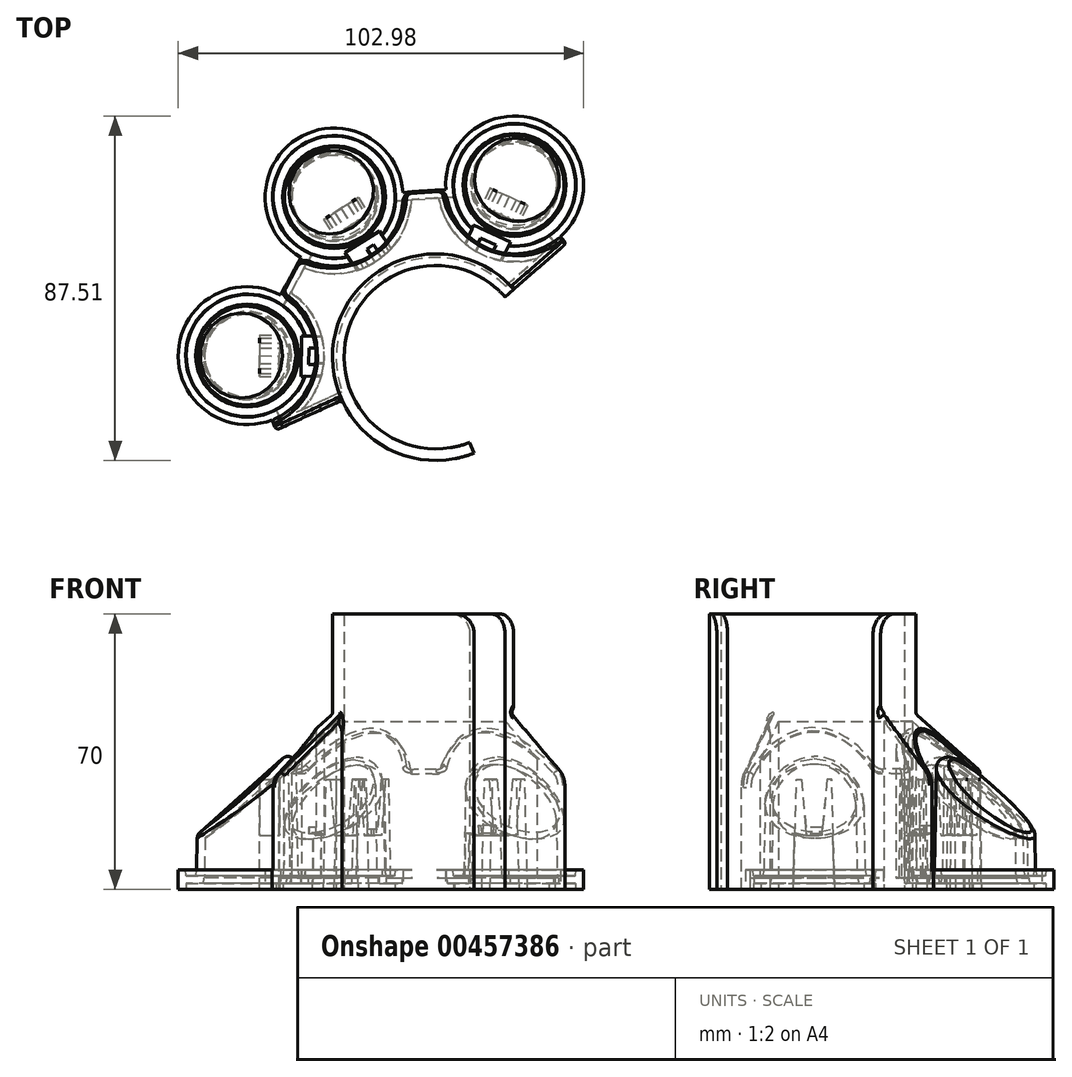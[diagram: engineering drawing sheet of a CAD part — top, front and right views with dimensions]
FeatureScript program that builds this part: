
annotation { "Feature Type Name" : "Feature", "Feature Type Description" : "" }
export const myFeature = defineFeature(function(context is Context, id is Id, definition is map)
    precondition{}
    {
        {
            var Q0;
            Q0=qCreatedBy(makeId("Top.planeOp"),FACE);
            var sketch = newSketch(context, id + "F0", { "sketchPlane" : qUnion([Q0])});
            skCircle(sketch, "E0", {"center": v(0, 0) * mm, "radius": 23.31 * mm});
            skCircle(sketch, "E1", {"center": v(0, 0) * mm, "radius": 26.24 * mm});
            skCircle(sketch, "E2", {"center": v(-47.92, 0.4) * mm, "radius": 12.92 * mm});
            skCircle(sketch, "E3", {"center": v(-47.92, 0.4) * mm, "radius": 17.52 * mm});
            skCircle(sketch, "E4.1.0", {"center": v(-25.82, 40.7) * mm, "radius": 17.52 * mm});
            skCircle(sketch, "E4.1.1", {"center": v(-25.82, 40.7) * mm, "radius": 12.92 * mm});
            skCircle(sketch, "E4.2.0", {"center": v(20.02, 43.75) * mm, "radius": 17.52 * mm});
            skCircle(sketch, "E4.2.1", {"center": v(20.02, 43.75) * mm, "radius": 12.92 * mm});
            skPoint(sketch, "E4.center", {"position": v(-0.1, 0.38) * mm});
            skLineSegment(sketch, "E4.anchor1", {"start": v(-0.1, 0.38) * mm, "end": v(-47.92, 0.4) * mm, "construction": true});
            skLineSegment(sketch, "E4.anchor2", {"start": v(-0.1, 0.38) * mm, "end": v(20.02, 43.75) * mm, "construction": true});
            skLineSegment(sketch, "E5", {"start": v(-39.5, 15.77) * mm, "end": v(-34.25, 25.33) * mm});
            skLineSegment(sketch, "E6", {"start": v(-8.34, 41.86) * mm, "end": v(2.54, 42.58) * mm});
            skLineSegment(sketch, "E7", {"start": v(17.58, 15.31) * mm, "end": v(19.79, 17.23) * mm});
            skLineSegment(sketch, "E8", {"start": v(8.61, -21.66) * mm, "end": v(9.7, -24.38) * mm});
            skLineSegment(sketch, "E9", {"start": v(31.65, 30.65) * mm, "end": v(33.19, 28.9) * mm});
            skLineSegment(sketch, "E10", {"start": v(33.19, 28.9) * mm, "end": v(19.79, 17.23) * mm});
            skLineSegment(sketch, "E11", {"start": v(-41.63, -15.94) * mm, "end": v(-40.62, -18.56) * mm});
            skLineSegment(sketch, "E12", {"start": v(-40.62, -18.56) * mm, "end": v(-23.87, -10.9) * mm});
            skLineSegment(sketch, "E13", {"start": v(-8.34, 41.86) * mm, "end": v(-34.25, 25.33) * mm});
            skSolve(sketch);
        }
        {
            var Q0;
            {var subQ0=sQuery(id+"F0.wireOp",EDGE,"E7");Q0=makeQuery(id+"F0.imprint","IMPRINT",FACE,{"disambiguationData":[TD([[makeQuery(id+"F0.imprint","IMPRINT",EDGE,{"derivedFrom":subQ0}),1.0]])]});}
            var Q1;
            {var subQ0=sQuery(id+"F0.wireOp",EDGE,"E5");Q1=makeQuery(id+"F0.imprint","IMPRINT",FACE,{"disambiguationData":[TD([[makeQuery(id+"F0.imprint","IMPRINT",EDGE,{"derivedFrom":subQ0}),-1.0]])]});}
            var Q2;
            Q2=makeQuery(id+"F0.imprint","IMPRINT",FACE,{"disambiguationData":[TD([[makeQuery(id+"F0.imprint","IMPRINT",EDGE,{"derivedFrom":sQuery(id+"F0.wireOp",EDGE,"E4.2.1")}),-1.0]])]});
            var Q3;
            Q3=makeQuery(id+"F0.imprint","IMPRINT",FACE,{"disambiguationData":[TD([[makeQuery(id+"F0.imprint","IMPRINT",EDGE,{"derivedFrom":sQuery(id+"F0.wireOp",EDGE,"E4.2.1")}),1.0]])]});
            var Q4;
            Q4=makeQuery(id+"F0.imprint","IMPRINT",FACE,{"disambiguationData":[TD([[makeQuery(id+"F0.imprint","IMPRINT",EDGE,{"derivedFrom":sQuery(id+"F0.wireOp",EDGE,"E4.1.1")}),-1.0]])]});
            var Q5;
            Q5=makeQuery(id+"F0.imprint","IMPRINT",FACE,{"disambiguationData":[TD([[makeQuery(id+"F0.imprint","IMPRINT",EDGE,{"derivedFrom":sQuery(id+"F0.wireOp",EDGE,"E4.1.1")}),1.0]])]});
            var Q6;
            Q6=makeQuery(id+"F0.imprint","IMPRINT",FACE,{"disambiguationData":[TD([[makeQuery(id+"F0.imprint","IMPRINT",EDGE,{"derivedFrom":sQuery(id+"F0.wireOp",EDGE,"E2")}),1.0]])]});
            var Q7;
            Q7=makeQuery(id+"F0.imprint","IMPRINT",FACE,{"disambiguationData":[TD([[makeQuery(id+"F0.imprint","IMPRINT",EDGE,{"derivedFrom":sQuery(id+"F0.wireOp",EDGE,"E2")}),-1.0]])]});
            extrude(context, id + "F1", {"entities" : qUnion([Q0, Q1, Q2, Q3, Q4, Q5, Q6, Q7]), "depth" : 5 * mm});
        }
        {
            var Q0;
            {var subQ5=sQuery(id+"F0.wireOp",EDGE,"zP7nwWVG-uyIf-8n9z-kM4t-hGhugBOlDqZd");Q0=makeQuery(id+"F0.imprint","IMPRINT",FACE,{"disambiguationData":[TD([[makeQuery(id+"F0.imprint","IMPRINT",EDGE,{"derivedFrom":subQ5}),-1.0]])]});}
            var Q1;
            {var subQ4=sQuery(id+"F0.wireOp",EDGE,"E7");Q1=makeQuery(id+"F0.imprint","IMPRINT",FACE,{"disambiguationData":[TD([[makeQuery(id+"F0.imprint","IMPRINT",EDGE,{"derivedFrom":subQ4}),1.0]])]});}
            var Q2;
            {var subQ0=sQuery(id+"F0.wireOp",EDGE,"E0");var subQ1=makeQuery(id+"F0.imprint","INTERSECT",VERTEX,{"derivedFrom":[subQ0,sQuery(id+"F0.wireOp",EDGE,"E7")]});Q2=makeQuery(id+"F0.imprint","IMPRINT",FACE,{"disambiguationData":[TD([[makeQuery(id+"F0.imprint","IMPRINT",EDGE,{"disambiguationData":[TD([[subQ1,-1.0]])],"derivedFrom":subQ0}),1.0]])]});}
            var Q3;
            {var subQ0=sQuery(id+"F0.wireOp",EDGE,"E5");Q3=makeQuery(id+"F0.imprint","IMPRINT",FACE,{"disambiguationData":[TD([[makeQuery(id+"F0.imprint","IMPRINT",EDGE,{"derivedFrom":subQ0}),-1.0]])]});}
            var Q4;
            Q4=makeQuery(id+"F1.opExtrude","CAP_FACE",FACE,{"disambiguationData":[OSD([sQuery(id+"F0.wireOp",EDGE,"E1"),sQuery(id+"F0.wireOp",EDGE,"E3"),sQuery(id+"F0.wireOp",EDGE,"E4.1.0"),sQuery(id+"F0.wireOp",EDGE,"E4.2.0"),sQuery(id+"F0.wireOp",EDGE,"zP7nwWVG-uyIf-8n9z-kM4t-hGhugBOlDqZd"),sQuery(id+"F0.wireOp",EDGE,"U5mlmDiE-PqSx-qM5O-4Tfx-D3ZpNaptZaIW"),sQuery(id+"F0.wireOp",EDGE,"E5"),sQuery(id+"F0.wireOp",EDGE,"E6")])],"isStart":false});
            extrude(context, id + "F2", {"entities" : qUnion([Q0, Q1, Q2, Q3]), "operationType" : NewBodyOperationType.ADD, "depth" : 70 * mm, "hasSecondDirection" : true, "secondDirectionBound" : SecondDirectionBoundingType.UP_TO_SURFACE, "secondDirectionOppositeDirection" : false, "secondDirectionBoundEntityFace" : qUnion([Q4]), "secondDirectionDepth" : 25 * mm});
        }
        {
            var Q0;
            Q0=makeQuery(id+"F0.imprint","IMPRINT",FACE,{"disambiguationData":[TD([[makeQuery(id+"F0.imprint","IMPRINT",EDGE,{"derivedFrom":sQuery(id+"F0.wireOp",EDGE,"E4.2.1")}),1.0]])]});
            var Q1;
            Q1=makeQuery(id+"F0.imprint","IMPRINT",FACE,{"disambiguationData":[TD([[makeQuery(id+"F0.imprint","IMPRINT",EDGE,{"derivedFrom":sQuery(id+"F0.wireOp",EDGE,"E4.1.1")}),1.0]])]});
            var Q2;
            Q2=makeQuery(id+"F0.imprint","IMPRINT",FACE,{"disambiguationData":[TD([[makeQuery(id+"F0.imprint","IMPRINT",EDGE,{"derivedFrom":sQuery(id+"F0.wireOp",EDGE,"E2")}),1.0]])]});
            extrude(context, id + "F3", {"entities" : qUnion([Q0, Q1, Q2]), "operationType" : NewBodyOperationType.ADD, "depth" : 53.8 * mm, "hasDraft" : true, "draftAngle" : 1 * degree, "draftPullDirection" : true});
        }
        {
            var Q0;
            {var subQ0=sQuery(id+"F0.wireOp",EDGE,"E0");var subQ1=makeQuery(id+"F0.imprint","INTERSECT",VERTEX,{"derivedFrom":[subQ0,sQuery(id+"F0.wireOp",EDGE,"E7")]});Q0=makeQuery(id+"F0.imprint","IMPRINT",FACE,{"disambiguationData":[TD([[makeQuery(id+"F0.imprint","IMPRINT",EDGE,{"disambiguationData":[TD([[subQ1,-1.0]])],"derivedFrom":subQ0}),1.0]])]});}
            var Q1;
            Q1=sQuery(id+"F0.wireOp",EDGE,"E0");
            extrude(context, id + "F4", {"entities" : qUnion([Q0]), "operationType" : NewBodyOperationType.REMOVE, "surfaceEntities" : qUnion([Q1]), "endBound" : BoundingType.THROUGH_ALL, "depth" : 25 * mm});
        }
        {
            var Q0;
            {var subQ0=sQuery(id+"F0.wireOp",EDGE,"E10");var subQ1=sQuery(id+"F0.wireOp",EDGE,"E7");Q0=makeQuery(id+"F2.boolean.opBoolean","MERGE",FACE,{"derivedFrom":[makeQuery(id+"F1.opExtrude","SWEPT_FACE",FACE,{"disambiguationData":[OSD([subQ1,subQ0])]}),makeQuery(id+"F2.opExtrude","SWEPT_FACE",FACE,{"disambiguationData":[OSD([subQ1,subQ0])]})]});}
            var sketch = newSketch(context, id + "F5", { "sketchPlane" : qUnion([Q0])});
            skLineSegment(sketch, "E14", {"start": v(26.24, 44.56) * mm, "end": v(67.38, 7.9) * mm});
            skLineSegment(sketch, "E15", {"start": v(67.38, 7.9) * mm, "end": v(67.38, 70) * mm});
            skLineSegment(sketch, "E16", {"start": v(67.38, 70) * mm, "end": v(26.24, 70) * mm});
            skLineSegment(sketch, "E17", {"start": v(26.24, 44.56) * mm, "end": v(26.24, 70) * mm});
            skPoint(sketch, "E18.0.end.orphan", {"position": v(26.24, 0) * mm});
            skPoint(sketch, "E18.0.start.orphan", {"position": v(-26.24, 0) * mm});
            skSolve(sketch);
        }
        {
            var Q0;
            {var subQ0=sQuery(id+"F5.wireOp",EDGE,"E17");Q0=makeQuery(id+"F5.imprint","IMPRINT",FACE,{"disambiguationData":[TD([[makeQuery(id+"F5.imprint","IMPRINT",EDGE,{"derivedFrom":subQ0}),-1.0]])]});}
            var Q1;
            {var subQ0=sQuery(id+"F5.wireOp",EDGE,"E15");Q1=makeQuery(id+"F5.imprint","IMPRINT",FACE,{"disambiguationData":[TD([[makeQuery(id+"F5.imprint","IMPRINT",EDGE,{"derivedFrom":subQ0}),1.0]])]});}
            var Q2;
            Q2=sQuery(id+"F0.wireOp",EDGE,"E0");
            revolve(context, id + "F6", {"operationType" : NewBodyOperationType.REMOVE, "entities" : qUnion([Q0, Q1]), "axis" : qUnion([Q2]), "revolveType" : RevolveType.FULL, "oppositeDirection" : true});
        }
        {
            var Q0;
            Q0=sQuery(id+"F0.wireOp",EDGE,"E13");
            extrude(context, id + "F7", {"bodyType" : ToolBodyType.SURFACE, "surfaceEntities" : qUnion([Q0]), "depth" : 101.5 * mm});
        }
        {
            var Q0;
            Q0=makeQuery(id+"F7.opExtrude","SWEPT_FACE",FACE,{"disambiguationData":[OSD([sQuery(id+"F0.wireOp",EDGE,"E13")])]});
            var sketch = newSketch(context, id + "F8", { "sketchPlane" : qUnion([Q0])});
            skFitSpline(sketch, "E19.0.0", {"points": [v(1.38, 35.88) * mm, v(0.16, 35.97) * mm, v(-0.81, 35.93) * mm, v(-1.76, 35.84) * mm, v(-2.69, 35.64) * mm, v(-3.59, 35.36) * mm, v(-4.45, 35.04) * mm, v(-5.47, 34.55) * mm, v(-6.6, 33.86) * mm, v(-7.6, 33.1) * mm, v(-8.52, 32.28) * mm, v(-9.34, 31.4) * mm, v(-10.07, 30.5) * mm, v(-10.9, 29.28) * mm, v(-11.57, 28.03) * mm, v(-12.06, 26.75) * mm, v(-12.43, 25.47) * mm, v(-12.62, 24.2) * mm, v(-12.63, 22.96) * mm, v(-12.5, 21.71) * mm, v(-12.1, 20.23) * mm, v(-11.37, 18.83) * mm, v(-10.53, 17.76) * mm, v(-9.8, 17) * mm, v(-9.1, 16.43) * mm, v(-8.47, 16) * mm, v(-7.8, 15.58) * mm, v(-6.9, 15.1) * mm, v(-5.93, 14.7) * mm, v(-5.09, 14.42) * mm, v(-4.21, 14.17) * mm, v(-3.1, 13.93) * mm, v(-1.7, 13.75) * mm, v(-0.23, 13.68) * mm, v(0.96, 13.72) * mm, v(1.91, 13.82) * mm, v(2.62, 13.91) * mm, v(3.32, 14.04) * mm, v(4.21, 14.25) * mm, v(5.29, 14.56) * mm, v(6.5, 15.04) * mm, v(7.59, 15.6) * mm, v(8.58, 16.23) * mm, v(9.45, 16.93) * mm, v(10.2, 17.67) * mm, v(10.84, 18.47) * mm, v(11.37, 19.3) * mm, v(11.78, 20.16) * mm, v(12.09, 21.05) * mm, v(12.3, 21.97) * mm, v(12.4, 22.9) * mm, v(12.4, 23.83) * mm, v(12.32, 24.78) * mm, v(12.14, 25.75) * mm, v(11.87, 26.7) * mm, v(11.39, 27.98) * mm, v(10.74, 29.23) * mm, v(9.9, 30.48) * mm, v(9.18, 31.38) * mm, v(8.37, 32.25) * mm, v(7.46, 33.07) * mm, v(6.44, 33.85) * mm, v(5.33, 34.53) * mm, v(4.3, 35.03) * mm, v(3.44, 35.36) * mm, v(2.54, 35.64) * mm, v(1.38, 35.88) * mm, v(0.16, 35.97) * mm, v(-0.81, 35.93) * mm, v(1.38, 35.88) * mm]});
            skLineSegment(sketch, "E20", {"start": v(-12.95, 5) * mm, "end": v(-12.62, 23.55) * mm});
            skLineSegment(sketch, "E21", {"start": v(12.4, 23.6) * mm, "end": v(12.72, 5) * mm});
            skLineSegment(sketch, "E22.0", {"start": v(-15.48, 0) * mm, "end": v(15.25, 0) * mm});
            skLineSegment(sketch, "E23", {"start": v(0, 45.7) * mm, "end": v(0, 0) * mm});
            skLineSegment(sketch, "E24", {"start": v(5.25, 0) * mm, "end": v(4.46, 28) * mm});
            skLineSegment(sketch, "E25", {"start": v(4.46, 28) * mm, "end": v(3.27, 27.98) * mm});
            skLineSegment(sketch, "E26", {"start": v(3.27, 27.98) * mm, "end": v(1.95, 13.8) * mm});
            skLineSegment(sketch, "E27", {"start": v(1.95, 13.8) * mm, "end": v(0, 13.77) * mm});
            skLineSegment(sketch, "E28.MirrorCS", {"start": v(-1.95, 13.8) * mm, "end": v(0, 13.77) * mm});
            skLineSegment(sketch, "E29.MirrorCS", {"start": v(-3.27, 27.98) * mm, "end": v(-1.95, 13.8) * mm});
            skLineSegment(sketch, "E30.MirrorCS", {"start": v(-4.46, 28) * mm, "end": v(-3.27, 27.98) * mm});
            skLineSegment(sketch, "E31.MirrorCS", {"start": v(-5.25, 0) * mm, "end": v(-4.46, 28) * mm});
            skLineSegment(sketch, "E32", {"start": v(-2.09, 15.29) * mm, "end": v(2.09, 15.29) * mm});
            skSolve(sketch);
        }
        {
            var Q0;
            Q0=makeQuery(id+"F2.opExtrude","SWEPT_EDGE",EDGE,{"disambiguationData":[OSD([sQuery(id+"F0.wireOp",EDGE,"E4.1.0"),sQuery(id+"F0.wireOp",EDGE,"E5"),sQuery(id+"F0.wireOp",EDGE,"E13")])]});
            var Q1;
            Q1=makeQuery(id+"F2.opExtrude","SWEPT_EDGE",EDGE,{"disambiguationData":[OSD([sQuery(id+"F0.wireOp",EDGE,"E4.1.0"),sQuery(id+"F0.wireOp",EDGE,"E6"),sQuery(id+"F0.wireOp",EDGE,"E13")])]});
            var Q2;
            Q2=makeQuery(id+"F2.opExtrude","SWEPT_EDGE",EDGE,{"disambiguationData":[OSD([sQuery(id+"F0.wireOp",EDGE,"E4.2.0"),sQuery(id+"F0.wireOp",EDGE,"E6")])]});
            var Q3;
            Q3=makeQuery(id+"F2.opExtrude","SWEPT_EDGE",EDGE,{"disambiguationData":[OSD([sQuery(id+"F0.wireOp",EDGE,"E3"),sQuery(id+"F0.wireOp",EDGE,"E5")])]});
            fillet(context, id + "F9", {"entities" : qUnion([Q0, Q1, Q2, Q3]), "radius" : 2.5 * mm, "tangentPropagation" : true, "allowEdgeOverflow" : false});
        }
        {
            var Q0;
            {var subQ0=sQuery(id+"F0.wireOp",EDGE,"E11");Q0=makeQuery(id+"F6.boolean.opBoolean","INTERSECT",EDGE,{"derivedFrom":[makeQuery(id+"F2.boolean.opBoolean","MERGE",FACE,{"derivedFrom":[makeQuery(id+"F1.opExtrude","SWEPT_FACE",FACE,{"disambiguationData":[OSD([subQ0])]}),makeQuery(id+"F2.opExtrude","SWEPT_FACE",FACE,{"disambiguationData":[OSD([subQ0])]})]}),makeQuery(id+"F6.opRevolve","SWEPT_FACE",FACE,{"disambiguationData":[OSD([sQuery(id+"F5.wireOp",EDGE,"E14")])]})]});}
            var Q1;
            {var subQ0=sQuery(id+"F0.wireOp",EDGE,"E9");Q1=makeQuery(id+"F6.boolean.opBoolean","INTERSECT",EDGE,{"derivedFrom":[makeQuery(id+"F2.boolean.opBoolean","MERGE",FACE,{"derivedFrom":[makeQuery(id+"F1.opExtrude","SWEPT_FACE",FACE,{"disambiguationData":[OSD([subQ0])]}),makeQuery(id+"F2.opExtrude","SWEPT_FACE",FACE,{"disambiguationData":[OSD([subQ0])]})]}),makeQuery(id+"F6.opRevolve","SWEPT_FACE",FACE,{"disambiguationData":[OSD([sQuery(id+"F5.wireOp",EDGE,"E14")])]})]});}
            var Q2;
            Q2=makeQuery(id+"F2.opExtrude","CAP_EDGE",EDGE,{"disambiguationData":[OSD([sQuery(id+"F0.wireOp",EDGE,"E7"),sQuery(id+"F0.wireOp",EDGE,"E10")])],"isStart":false});
            var Q3;
            Q3=makeQuery(id+"F2.opExtrude","CAP_EDGE",EDGE,{"disambiguationData":[OSD([sQuery(id+"F0.wireOp",EDGE,"E8")])],"isStart":false});
            fillet(context, id + "F10", {"entities" : qUnion([Q0, Q1, Q2, Q3]), "radius" : 5 * mm, "tangentPropagation" : true, "allowEdgeOverflow" : false});
        }
        {
            var Q0;
            {var subQ0=sQuery(id+"F0.wireOp",EDGE,"E1");Q0=makeQuery(id+"F6.boolean.opBoolean","COPY",FACE,{"disambiguationData":[TD([makeQuery(id+"F1.opExtrude","SWEPT_FACE",FACE,{"disambiguationData":[OSD([subQ0])]})])],"derivedFrom":makeQuery(id+"F6.opRevolve","SWEPT_FACE",FACE,{"disambiguationData":[OSD([sQuery(id+"F5.wireOp",EDGE,"E14")])]})});}
            fillet(context, id + "F11", {"entities" : qUnion([Q0]), "radius" : 1 * mm, "tangentPropagation" : true, "allowEdgeOverflow" : false});
        }
        {
            var Q0;
            Q0=makeQuery(id+"F6.boolean.opBoolean","COPY",FACE,{"disambiguationData":[TD([makeQuery(id+"F3.opExtrude","SWEPT_FACE",FACE,{"disambiguationData":[OSD([sQuery(id+"F0.wireOp",EDGE,"E2")])]})])],"derivedFrom":makeQuery(id+"F6.opRevolve","SWEPT_FACE",FACE,{"disambiguationData":[OSD([sQuery(id+"F5.wireOp",EDGE,"E14")])]})});
            var Q1;
            Q1=makeQuery(id+"F6.boolean.opBoolean","COPY",FACE,{"disambiguationData":[TD([makeQuery(id+"F3.opExtrude","SWEPT_FACE",FACE,{"disambiguationData":[OSD([sQuery(id+"F0.wireOp",EDGE,"E4.1.1")])]})])],"derivedFrom":makeQuery(id+"F6.opRevolve","SWEPT_FACE",FACE,{"disambiguationData":[OSD([sQuery(id+"F5.wireOp",EDGE,"E14")])]})});
            var Q2;
            Q2=makeQuery(id+"F6.boolean.opBoolean","COPY",FACE,{"disambiguationData":[TD([makeQuery(id+"F3.opExtrude","SWEPT_FACE",FACE,{"disambiguationData":[OSD([sQuery(id+"F0.wireOp",EDGE,"E4.2.1")])]})])],"derivedFrom":makeQuery(id+"F6.opRevolve","SWEPT_FACE",FACE,{"disambiguationData":[OSD([sQuery(id+"F5.wireOp",EDGE,"E14")])]})});
            fillet(context, id + "F12", {"entities" : qUnion([Q0, Q1, Q2]), "radius" : 2 * mm, "tangentPropagation" : true, "allowEdgeOverflow" : false});
        }
        {
            var Q0;
            {var subQ0=sQuery(id+"F0.wireOp",EDGE,"E11");var subQ1=sQuery(id+"F0.wireOp",EDGE,"E5");var subQ2=sQuery(id+"F0.wireOp",EDGE,"E3");Q0=makeQuery(id+"F2.boolean.opBoolean","SPLIT",FACE,{"disambiguationData":[TD([makeQuery(id+"F1.opExtrude","SWEPT_FACE",FACE,{"disambiguationData":[OSD([subQ2])]})])],"derivedFrom":makeQuery(id+"F1.opExtrude","CAP_FACE",FACE,{"disambiguationData":[OSD([sQuery(id+"F0.wireOp",EDGE,"E0"),sQuery(id+"F0.wireOp",EDGE,"E1"),subQ2,sQuery(id+"F0.wireOp",EDGE,"E4.1.0"),sQuery(id+"F0.wireOp",EDGE,"E4.2.0"),subQ1,sQuery(id+"F0.wireOp",EDGE,"E6"),sQuery(id+"F0.wireOp",EDGE,"E7"),sQuery(id+"F0.wireOp",EDGE,"E8"),sQuery(id+"F0.wireOp",EDGE,"E9"),sQuery(id+"F0.wireOp",EDGE,"E10"),subQ0,sQuery(id+"F0.wireOp",EDGE,"E12")])],"isStart":false})});}
            var sketch = newSketch(context, id + "F13", { "sketchPlane" : qUnion([Q0])});
            skArc(sketch, "E33.0.0", {"start": v(-39.5, 15.77) * mm, "mid": v(-65.4, 1.59) * mm, "end": v(-41.63, -15.94) * mm});
            skLineSegment(sketch, "E33.0.1", {"start": v(-41.63, -15.94) * mm, "end": v(-41.28, -16.85) * mm});
            skArc(sketch, "E33.0.2", {"start": v(-41.28, -16.85) * mm, "mid": v(-41.27, -16.1) * mm, "end": v(-40.76, -15.58) * mm});
            skArc(sketch, "E33.0.3", {"start": v(-40.76, -15.58) * mm, "mid": v(-30.5, -1.39) * mm, "end": v(-37.64, 14.6) * mm});
            skArc(sketch, "E33.0.4", {"start": v(-37.64, 14.6) * mm, "mid": v(-38.62, 16.07) * mm, "end": v(-38.37, 17.82) * mm});
            skLineSegment(sketch, "E33.0.5", {"start": v(-38.37, 17.82) * mm, "end": v(-39.5, 15.77) * mm});
            skArc(sketch, "E34.0.0", {"start": v(-8.34, 41.86) * mm, "mid": v(-35.25, 55.46) * mm, "end": v(-34.25, 25.33) * mm});
            skLineSegment(sketch, "E34.0.1", {"start": v(-34.25, 25.33) * mm, "end": v(-35.38, 23.28) * mm});
            skArc(sketch, "E34.0.2", {"start": v(-35.38, 23.28) * mm, "mid": v(-34.03, 24.42) * mm, "end": v(-32.27, 24.4) * mm});
            skArc(sketch, "E34.0.3", {"start": v(-32.27, 24.4) * mm, "mid": v(-16.4, 25.92) * mm, "end": v(-8.33, 39.67) * mm});
            skArc(sketch, "E34.0.4", {"start": v(-8.33, 39.67) * mm, "mid": v(-7.61, 41.28) * mm, "end": v(-6, 42.01) * mm});
            skLineSegment(sketch, "E34.0.5", {"start": v(-6, 42.01) * mm, "end": v(-8.34, 41.86) * mm});
            skArc(sketch, "E35.0.0", {"start": v(31.65, 30.65) * mm, "mid": v(26.67, 59.96) * mm, "end": v(2.54, 42.58) * mm});
            skLineSegment(sketch, "E35.0.1", {"start": v(2.54, 42.58) * mm, "end": v(0.2, 42.43) * mm});
            skArc(sketch, "E35.0.2", {"start": v(0.2, 42.43) * mm, "mid": v(1.9, 41.91) * mm, "end": v(2.82, 40.41) * mm});
            skArc(sketch, "E35.0.3", {"start": v(2.82, 40.41) * mm, "mid": v(13.95, 27.32) * mm, "end": v(30.92, 30.04) * mm});
            skArc(sketch, "E35.0.4", {"start": v(30.92, 30.04) * mm, "mid": v(31.63, 30.25) * mm, "end": v(32.3, 29.92) * mm});
            skLineSegment(sketch, "E35.0.5", {"start": v(32.3, 29.92) * mm, "end": v(31.65, 30.65) * mm});
            skCircle(sketch, "E36.0", {"center": v(-47.92, 0.4) * mm, "radius": 12.92 * mm});
            skCircle(sketch, "E37.0", {"center": v(-25.82, 40.7) * mm, "radius": 12.92 * mm});
            skCircle(sketch, "E38.0", {"center": v(20.02, 43.75) * mm, "radius": 12.92 * mm});
            skCircle(sketch, "E39.0", {"center": v(-47.92, 0.4) * mm, "radius": 15.62 * mm});
            skCircle(sketch, "E40.0", {"center": v(-25.82, 40.7) * mm, "radius": 15.62 * mm});
            skCircle(sketch, "E41.0", {"center": v(20.02, 43.75) * mm, "radius": 15.62 * mm});
            skSolve(sketch);
        }
        {
            var Q0;
            Q0=makeQuery(id+"F13.imprint","IMPRINT",FACE,{"disambiguationData":[TD([[makeQuery(id+"F13.imprint","IMPRINT",EDGE,{"derivedFrom":sQuery(id+"F13.wireOp",EDGE,"E38.0")}),-1.0]])]});
            var Q1;
            Q1=makeQuery(id+"F13.imprint","IMPRINT",FACE,{"disambiguationData":[TD([[makeQuery(id+"F13.imprint","IMPRINT",EDGE,{"derivedFrom":sQuery(id+"F13.wireOp",EDGE,"E37.0")}),-1.0]])]});
            var Q2;
            Q2=makeQuery(id+"F13.imprint","IMPRINT",FACE,{"disambiguationData":[TD([[makeQuery(id+"F13.imprint","IMPRINT",EDGE,{"derivedFrom":sQuery(id+"F13.wireOp",EDGE,"E36.0")}),-1.0]])]});
            extrude(context, id + "F14", {"entities" : qUnion([Q0, Q1, Q2]), "operationType" : NewBodyOperationType.REMOVE, "oppositeDirection" : true, "depth" : 1.5 * mm, "hasDraft" : true, "draftAngle" : 5 * degree, "draftPullDirection" : true});
        }
        {
            var Q0;
            Q0=makeQuery(id+"F1.opExtrude","CAP_FACE",FACE,{"disambiguationData":[OSD([sQuery(id+"F0.wireOp",EDGE,"E0"),sQuery(id+"F0.wireOp",EDGE,"E1"),sQuery(id+"F0.wireOp",EDGE,"E3"),sQuery(id+"F0.wireOp",EDGE,"E4.1.0"),sQuery(id+"F0.wireOp",EDGE,"E4.2.0"),sQuery(id+"F0.wireOp",EDGE,"E5"),sQuery(id+"F0.wireOp",EDGE,"E6"),sQuery(id+"F0.wireOp",EDGE,"E7"),sQuery(id+"F0.wireOp",EDGE,"E8"),sQuery(id+"F0.wireOp",EDGE,"E9"),sQuery(id+"F0.wireOp",EDGE,"E10"),sQuery(id+"F0.wireOp",EDGE,"E11"),sQuery(id+"F0.wireOp",EDGE,"E12")])],"isStart":true});
            shell(context, id + "F15", {"entities" : qUnion([Q0]), "thickness" : 2 * mm});
        }
        {
            var Q0;
            {var subQ0=sQuery(id+"F8.wireOp",EDGE,"E31.MirrorCS");var subQ1=sQuery(id+"F8.wireOp",EDGE,"E19.0.0");var subQ2=makeQuery(id+"F8.imprint","INTERSECT",VERTEX,{"derivedFrom":[subQ1,subQ0]});Q0=makeQuery(id+"F8.imprint","IMPRINT",FACE,{"disambiguationData":[TD([[makeQuery(id+"F8.imprint","IMPRINT",EDGE,{"disambiguationData":[TD([[subQ2,-1.0]])],"derivedFrom":subQ1}),-1.0]])]});}
            var Q1;
            {var subQ5=sQuery(id+"F8.wireOp",EDGE,"E25");Q1=makeQuery(id+"F8.imprint","IMPRINT",FACE,{"disambiguationData":[TD([[makeQuery(id+"F8.imprint","IMPRINT",EDGE,{"derivedFrom":subQ5}),1.0]])]});}
            var Q2;
            {var subQ0=sQuery(id+"F8.wireOp",EDGE,"E28.MirrorCS");Q2=makeQuery(id+"F8.imprint","IMPRINT",FACE,{"disambiguationData":[TD([[makeQuery(id+"F8.imprint","IMPRINT",EDGE,{"derivedFrom":subQ0}),-1.0]])]});}
            var Q3;
            {var subQ0=sQuery(id+"F8.wireOp",EDGE,"E23");var subQ5=sQuery(id+"F8.wireOp",EDGE,"E19.0.0");var subQ6=makeQuery(id+"F8.imprint","INTERSECT",VERTEX,{"disambiguationData":[OD(1.0)],"derivedFrom":[subQ5,subQ0]});Q3=makeQuery(id+"F8.imprint","IMPRINT",FACE,{"disambiguationData":[TD([[makeQuery(id+"F8.imprint","IMPRINT",EDGE,{"disambiguationData":[TD([[subQ6,-1.0]])],"derivedFrom":subQ5}),-1.0]])]});}
            var Q4;
            Q4=sQuery(id+"F8.wireOp",EDGE,"E24");
            extrude(context, id + "F16", {"entities" : qUnion([Q0, Q1, Q2, Q3]), "surfaceEntities" : qUnion([Q4]), "depth" : 5 * mm});
        }
        {
            var Q0;
            Q0=makeQuery(id+"F16.opExtrude","SWEPT_BODY",BODY,{"disambiguationData":[OSD([sQuery(id+"F8.wireOp",EDGE,"E19.0.0"),sQuery(id+"F8.wireOp",EDGE,"E22.0"),sQuery(id+"F8.wireOp",EDGE,"E23"),sQuery(id+"F8.wireOp",EDGE,"E24"),sQuery(id+"F8.wireOp",EDGE,"E25"),sQuery(id+"F8.wireOp",EDGE,"E26"),sQuery(id+"F8.wireOp",EDGE,"E27"),sQuery(id+"F8.wireOp",EDGE,"E28.MirrorCS"),sQuery(id+"F8.wireOp",EDGE,"E29.MirrorCS"),sQuery(id+"F8.wireOp",EDGE,"E30.MirrorCS"),sQuery(id+"F8.wireOp",EDGE,"E31.MirrorCS")])]});
            var Q1;
            Q1=sQuery(id+"F0.wireOp",EDGE,"E0");
            circularPattern(context, id + "F17", {"entities" : qUnion([Q0]), "axis" : qUnion([Q1]), "angle" : 57 * degree, "instanceCount" : 2, "equalSpace" : true});
        }
        {
            var Q0;
            Q0=makeQuery(id+"F16.opExtrude","SWEPT_BODY",BODY,{"disambiguationData":[OSD([sQuery(id+"F8.wireOp",EDGE,"E19.0.0"),sQuery(id+"F8.wireOp",EDGE,"E22.0"),sQuery(id+"F8.wireOp",EDGE,"E23"),sQuery(id+"F8.wireOp",EDGE,"E24"),sQuery(id+"F8.wireOp",EDGE,"E25"),sQuery(id+"F8.wireOp",EDGE,"E26"),sQuery(id+"F8.wireOp",EDGE,"E27"),sQuery(id+"F8.wireOp",EDGE,"E28.MirrorCS"),sQuery(id+"F8.wireOp",EDGE,"E29.MirrorCS"),sQuery(id+"F8.wireOp",EDGE,"E30.MirrorCS"),sQuery(id+"F8.wireOp",EDGE,"E31.MirrorCS")])]});
            var Q1;
            Q1=sQuery(id+"F0.wireOp",EDGE,"E0");
            circularPattern(context, id + "F18", {"entities" : qUnion([Q0]), "axis" : qUnion([Q1]), "angle" : 303 * degree, "instanceCount" : 2, "equalSpace" : true});
        }
        {
            var Q0;
            Q0=makeQuery(id+"F17.opPattern","COPY",FACE,{"derivedFrom":makeQuery(id+"F16.opExtrude","CAP_FACE",FACE,{"disambiguationData":[OSD([sQuery(id+"F8.wireOp",EDGE,"E19.0.0"),sQuery(id+"F8.wireOp",EDGE,"E22.0"),sQuery(id+"F8.wireOp",EDGE,"E23"),sQuery(id+"F8.wireOp",EDGE,"E24"),sQuery(id+"F8.wireOp",EDGE,"E25"),sQuery(id+"F8.wireOp",EDGE,"E26"),sQuery(id+"F8.wireOp",EDGE,"E27"),sQuery(id+"F8.wireOp",EDGE,"E28.MirrorCS"),sQuery(id+"F8.wireOp",EDGE,"E29.MirrorCS"),sQuery(id+"F8.wireOp",EDGE,"E30.MirrorCS"),sQuery(id+"F8.wireOp",EDGE,"E31.MirrorCS")])],"isStart":false}),"instanceName":"1"});
            var sketch = newSketch(context, id + "F19", { "sketchPlane" : qUnion([Q0])});
            skLineSegment(sketch, "E42.0.0", {"start": v(-4.46, 28) * mm, "end": v(-5.25, 0) * mm});
            skLineSegment(sketch, "E42.0.1", {"start": v(-5.25, 0) * mm, "end": v(5.25, 0) * mm});
            skLineSegment(sketch, "E42.0.2", {"start": v(5.25, 0) * mm, "end": v(4.46, 28) * mm});
            skLineSegment(sketch, "E42.0.3", {"start": v(4.46, 28) * mm, "end": v(3.27, 27.98) * mm});
            skLineSegment(sketch, "E42.0.4", {"start": v(3.27, 27.98) * mm, "end": v(1.95, 13.8) * mm});
            skLineSegment(sketch, "E42.0.5", {"start": v(1.95, 13.8) * mm, "end": v(1.67, 13.8) * mm});
            skFitSpline(sketch, "E42.0.6", {"points": [v(-0.08, 35.95) * mm, v(0.4, 35.95) * mm, v(1.38, 35.88) * mm, v(2.54, 35.64) * mm, v(3.44, 35.36) * mm, v(4.3, 35.03) * mm, v(5.33, 34.53) * mm, v(6.44, 33.85) * mm, v(7.46, 33.07) * mm, v(8.37, 32.25) * mm, v(9.18, 31.38) * mm, v(9.9, 30.48) * mm, v(10.74, 29.23) * mm, v(11.39, 27.98) * mm, v(11.87, 26.7) * mm, v(12.14, 25.75) * mm, v(12.32, 24.78) * mm, v(12.4, 23.83) * mm, v(12.4, 22.9) * mm, v(12.3, 21.97) * mm, v(12.09, 21.05) * mm, v(11.78, 20.16) * mm, v(11.37, 19.3) * mm, v(10.84, 18.47) * mm, v(10.2, 17.67) * mm, v(9.45, 16.93) * mm, v(8.58, 16.23) * mm, v(7.59, 15.6) * mm, v(6.5, 15.04) * mm, v(5.29, 14.56) * mm, v(4.21, 14.25) * mm, v(3.32, 14.04) * mm, v(2.62, 13.91) * mm, v(1.91, 13.82) * mm, v(0.96, 13.72) * mm, v(-0.23, 13.68) * mm, v(-1.7, 13.75) * mm, v(-3.1, 13.93) * mm, v(-4.21, 14.17) * mm, v(-5.09, 14.42) * mm, v(-5.93, 14.7) * mm, v(-6.9, 15.1) * mm, v(-7.8, 15.58) * mm, v(-8.47, 16) * mm, v(-9.1, 16.43) * mm, v(-9.8, 17) * mm, v(-10.53, 17.76) * mm, v(-11.37, 18.83) * mm, v(-12.1, 20.23) * mm, v(-12.5, 21.71) * mm, v(-12.63, 22.96) * mm, v(-12.62, 24.2) * mm, v(-12.43, 25.47) * mm, v(-12.06, 26.75) * mm, v(-11.57, 28.03) * mm, v(-10.9, 29.28) * mm, v(-10.07, 30.5) * mm, v(-9.34, 31.4) * mm, v(-8.52, 32.28) * mm, v(-7.6, 33.1) * mm, v(-6.6, 33.86) * mm, v(-5.47, 34.55) * mm, v(-4.45, 35.04) * mm, v(-3.59, 35.36) * mm, v(-2.69, 35.64) * mm, v(-1.76, 35.84) * mm, v(-0.81, 35.93) * mm, v(-0.33, 35.95) * mm, v(-0.08, 35.95) * mm]});
            skLineSegment(sketch, "E42.0.7", {"start": v(0, 13.7) * mm, "end": v(0, 13.77) * mm});
            skLineSegment(sketch, "E42.0.8", {"start": v(0, 13.77) * mm, "end": v(-1.95, 13.8) * mm});
            skLineSegment(sketch, "E42.0.9", {"start": v(-1.95, 13.8) * mm, "end": v(-3.27, 27.98) * mm});
            skLineSegment(sketch, "E42.0.10", {"start": v(-3.27, 27.98) * mm, "end": v(-4.46, 28) * mm});
            skLineSegment(sketch, "E43", {"start": v(-1.98, 14.15) * mm, "end": v(1.98, 14.15) * mm});
            skLineSegment(sketch, "E44", {"start": v(-2.13, 15.71) * mm, "end": v(2.13, 15.71) * mm});
            skSolve(sketch);
        }
        {
            var Q0;
            Q0=makeQuery(id+"F18.opPattern","COPY",FACE,{"derivedFrom":makeQuery(id+"F16.opExtrude","CAP_FACE",FACE,{"disambiguationData":[OSD([sQuery(id+"F8.wireOp",EDGE,"E19.0.0"),sQuery(id+"F8.wireOp",EDGE,"E22.0"),sQuery(id+"F8.wireOp",EDGE,"E23"),sQuery(id+"F8.wireOp",EDGE,"E24"),sQuery(id+"F8.wireOp",EDGE,"E25"),sQuery(id+"F8.wireOp",EDGE,"E26"),sQuery(id+"F8.wireOp",EDGE,"E27"),sQuery(id+"F8.wireOp",EDGE,"E28.MirrorCS"),sQuery(id+"F8.wireOp",EDGE,"E29.MirrorCS"),sQuery(id+"F8.wireOp",EDGE,"E30.MirrorCS"),sQuery(id+"F8.wireOp",EDGE,"E31.MirrorCS")])],"isStart":false}),"instanceName":"1"});
            var sketch = newSketch(context, id + "F20", { "sketchPlane" : qUnion([Q0])});
            skLineSegment(sketch, "E45.0.0", {"start": v(-4.46, 28) * mm, "end": v(-5.25, 0) * mm});
            skLineSegment(sketch, "E45.0.1", {"start": v(-5.25, 0) * mm, "end": v(5.25, 0) * mm});
            skLineSegment(sketch, "E45.0.2", {"start": v(5.25, 0) * mm, "end": v(4.46, 28) * mm});
            skLineSegment(sketch, "E45.0.3", {"start": v(4.46, 28) * mm, "end": v(3.27, 27.98) * mm});
            skLineSegment(sketch, "E45.0.4", {"start": v(3.27, 27.98) * mm, "end": v(1.95, 13.8) * mm});
            skLineSegment(sketch, "E45.0.5", {"start": v(1.95, 13.8) * mm, "end": v(1.67, 13.8) * mm});
            skFitSpline(sketch, "E45.0.6", {"points": [v(-0.08, 35.95) * mm, v(0.4, 35.95) * mm, v(1.38, 35.88) * mm, v(2.54, 35.64) * mm, v(3.44, 35.36) * mm, v(4.3, 35.03) * mm, v(5.33, 34.53) * mm, v(6.44, 33.85) * mm, v(7.46, 33.07) * mm, v(8.37, 32.25) * mm, v(9.18, 31.38) * mm, v(9.9, 30.48) * mm, v(10.74, 29.23) * mm, v(11.39, 27.98) * mm, v(11.87, 26.7) * mm, v(12.14, 25.75) * mm, v(12.32, 24.78) * mm, v(12.4, 23.83) * mm, v(12.4, 22.9) * mm, v(12.3, 21.97) * mm, v(12.09, 21.05) * mm, v(11.78, 20.16) * mm, v(11.37, 19.3) * mm, v(10.84, 18.47) * mm, v(10.2, 17.67) * mm, v(9.45, 16.93) * mm, v(8.58, 16.23) * mm, v(7.59, 15.6) * mm, v(6.5, 15.04) * mm, v(5.29, 14.56) * mm, v(4.21, 14.25) * mm, v(3.32, 14.04) * mm, v(2.62, 13.91) * mm, v(1.91, 13.82) * mm, v(0.96, 13.72) * mm, v(-0.23, 13.68) * mm, v(-1.7, 13.75) * mm, v(-3.1, 13.93) * mm, v(-4.21, 14.17) * mm, v(-5.09, 14.42) * mm, v(-5.93, 14.7) * mm, v(-6.9, 15.1) * mm, v(-7.8, 15.58) * mm, v(-8.47, 16) * mm, v(-9.1, 16.43) * mm, v(-9.8, 17) * mm, v(-10.53, 17.76) * mm, v(-11.37, 18.83) * mm, v(-12.1, 20.23) * mm, v(-12.5, 21.71) * mm, v(-12.63, 22.96) * mm, v(-12.62, 24.2) * mm, v(-12.43, 25.47) * mm, v(-12.06, 26.75) * mm, v(-11.57, 28.03) * mm, v(-10.9, 29.28) * mm, v(-10.07, 30.5) * mm, v(-9.34, 31.4) * mm, v(-8.52, 32.28) * mm, v(-7.6, 33.1) * mm, v(-6.6, 33.86) * mm, v(-5.47, 34.55) * mm, v(-4.45, 35.04) * mm, v(-3.59, 35.36) * mm, v(-2.69, 35.64) * mm, v(-1.76, 35.84) * mm, v(-0.81, 35.93) * mm, v(-0.33, 35.95) * mm, v(-0.08, 35.95) * mm]});
            skLineSegment(sketch, "E45.0.7", {"start": v(0, 13.7) * mm, "end": v(0, 13.77) * mm});
            skLineSegment(sketch, "E45.0.8", {"start": v(0, 13.77) * mm, "end": v(-1.95, 13.8) * mm});
            skLineSegment(sketch, "E45.0.9", {"start": v(-1.95, 13.8) * mm, "end": v(-3.27, 27.98) * mm});
            skLineSegment(sketch, "E45.0.10", {"start": v(-3.27, 27.98) * mm, "end": v(-4.46, 28) * mm});
            skLineSegment(sketch, "E46", {"start": v(-2.18, 16.28) * mm, "end": v(2.18, 16.28) * mm});
            skLineSegment(sketch, "E47", {"start": v(-1.98, 14.2) * mm, "end": v(1.98, 14.2) * mm});
            skSolve(sketch);
        }
        {
            var Q0;
            {var subQ0=sQuery(id+"F8.wireOp",EDGE,"E28.MirrorCS");Q0=makeQuery(id+"F8.imprint","IMPRINT",FACE,{"disambiguationData":[TD([[makeQuery(id+"F8.imprint","IMPRINT",EDGE,{"derivedFrom":subQ0}),-1.0]])]});}
            var Q1;
            {var subQ5=sQuery(id+"F8.wireOp",EDGE,"E25");Q1=makeQuery(id+"F8.imprint","IMPRINT",FACE,{"disambiguationData":[TD([[makeQuery(id+"F8.imprint","IMPRINT",EDGE,{"derivedFrom":subQ5}),1.0]])]});}
            var Q2;
            {var subQ0=sQuery(id+"F8.wireOp",EDGE,"E23");var subQ5=sQuery(id+"F8.wireOp",EDGE,"E19.0.0");var subQ6=makeQuery(id+"F8.imprint","INTERSECT",VERTEX,{"disambiguationData":[OD(1.0)],"derivedFrom":[subQ5,subQ0]});Q2=makeQuery(id+"F8.imprint","IMPRINT",FACE,{"disambiguationData":[TD([[makeQuery(id+"F8.imprint","IMPRINT",EDGE,{"disambiguationData":[TD([[subQ6,-1.0]])],"derivedFrom":subQ5}),-1.0]])]});}
            var Q3;
            {var subQ0=sQuery(id+"F8.wireOp",EDGE,"E31.MirrorCS");var subQ1=sQuery(id+"F8.wireOp",EDGE,"E19.0.0");var subQ2=makeQuery(id+"F8.imprint","INTERSECT",VERTEX,{"derivedFrom":[subQ1,subQ0]});Q3=makeQuery(id+"F8.imprint","IMPRINT",FACE,{"disambiguationData":[TD([[makeQuery(id+"F8.imprint","IMPRINT",EDGE,{"disambiguationData":[TD([[subQ2,-1.0]])],"derivedFrom":subQ1}),-1.0]])]});}
            extrude(context, id + "F21", {"entities" : qUnion([Q0, Q1, Q2, Q3]), "operationType" : NewBodyOperationType.REMOVE, "oppositeDirection" : true, "depth" : 12.2 * mm, "hasSecondDirection" : true, "secondDirectionOppositeDirection" : true, "secondDirectionDepth" : 5 * mm});
        }
        {
            var Q0;
            Q0=makeQuery(id+"F19.imprint","IMPRINT",FACE,{"disambiguationData":[TD([[makeQuery(id+"F19.imprint","IMPRINT",EDGE,{"derivedFrom":sQuery(id+"F19.wireOp",EDGE,"E42.0.0")}),-1.0]])]});
            extrude(context, id + "F22", {"entities" : qUnion([Q0]), "operationType" : NewBodyOperationType.REMOVE, "oppositeDirection" : true, "depth" : 17.4 * mm, "hasSecondDirection" : true, "secondDirectionOppositeDirection" : true, "secondDirectionDepth" : 10.6 * mm});
        }
        {
            var Q0;
            Q0=makeQuery(id+"F20.imprint","IMPRINT",FACE,{"disambiguationData":[TD([[makeQuery(id+"F20.imprint","IMPRINT",EDGE,{"derivedFrom":sQuery(id+"F20.wireOp",EDGE,"E45.0.0")}),-1.0]])]});
            extrude(context, id + "F23", {"entities" : qUnion([Q0]), "operationType" : NewBodyOperationType.REMOVE, "oppositeDirection" : true, "depth" : 17.5 * mm, "hasSecondDirection" : true, "secondDirectionOppositeDirection" : true, "secondDirectionDepth" : 10.3 * mm});
        }
        {
            var Q0;
            {var subQ0=sQuery(id+"F20.wireOp",EDGE,"E46");Q0=makeQuery(id+"F20.imprint","IMPRINT",FACE,{"disambiguationData":[TD([[makeQuery(id+"F20.imprint","IMPRINT",EDGE,{"derivedFrom":subQ0}),-1.0]])]});}
            extrude(context, id + "F24", {"entities" : qUnion([Q0]), "operationType" : NewBodyOperationType.ADD, "oppositeDirection" : true, "depth" : 14.77 * mm, "hasSecondDirection" : true, "secondDirectionOppositeDirection" : true, "secondDirectionDepth" : 12.5 * mm});
        }
        {
            var Q0;
            {var subQ0=sQuery(id+"F19.wireOp",EDGE,"E43");Q0=makeQuery(id+"F19.imprint","IMPRINT",FACE,{"disambiguationData":[TD([[makeQuery(id+"F19.imprint","IMPRINT",EDGE,{"derivedFrom":subQ0}),1.0]])]});}
            extrude(context, id + "F25", {"entities" : qUnion([Q0]), "operationType" : NewBodyOperationType.ADD, "oppositeDirection" : true, "depth" : 15.1 * mm, "hasSecondDirection" : true, "secondDirectionOppositeDirection" : true, "secondDirectionDepth" : 12.5 * mm});
        }
        {
            var Q0;
            {var subQ3=sQuery(id+"F8.wireOp",EDGE,"E19.0.0");var subQ7=sQuery(id+"F8.wireOp",EDGE,"E27");var subQ9=makeQuery(id+"F8.imprint","INTERSECT",VERTEX,{"derivedFrom":[subQ3,subQ7]});Q0=makeQuery(id+"F8.imprint","IMPRINT",FACE,{"disambiguationData":[TD([[makeQuery(id+"F8.imprint","IMPRINT",EDGE,{"disambiguationData":[TD([[subQ9,-1.0]])],"derivedFrom":subQ3}),1.0]])]});}
            var Q1;
            {var subQ0=sQuery(id+"F8.wireOp",EDGE,"E28.MirrorCS");Q1=makeQuery(id+"F8.imprint","IMPRINT",FACE,{"disambiguationData":[TD([[makeQuery(id+"F8.imprint","IMPRINT",EDGE,{"derivedFrom":subQ0}),1.0]])]});}
            extrude(context, id + "F26", {"entities" : qUnion([Q0, Q1]), "operationType" : NewBodyOperationType.ADD, "oppositeDirection" : true, "depth" : 9.5 * mm, "hasSecondDirection" : true, "secondDirectionOppositeDirection" : true, "secondDirectionDepth" : 7.2 * mm});
        }
    });
